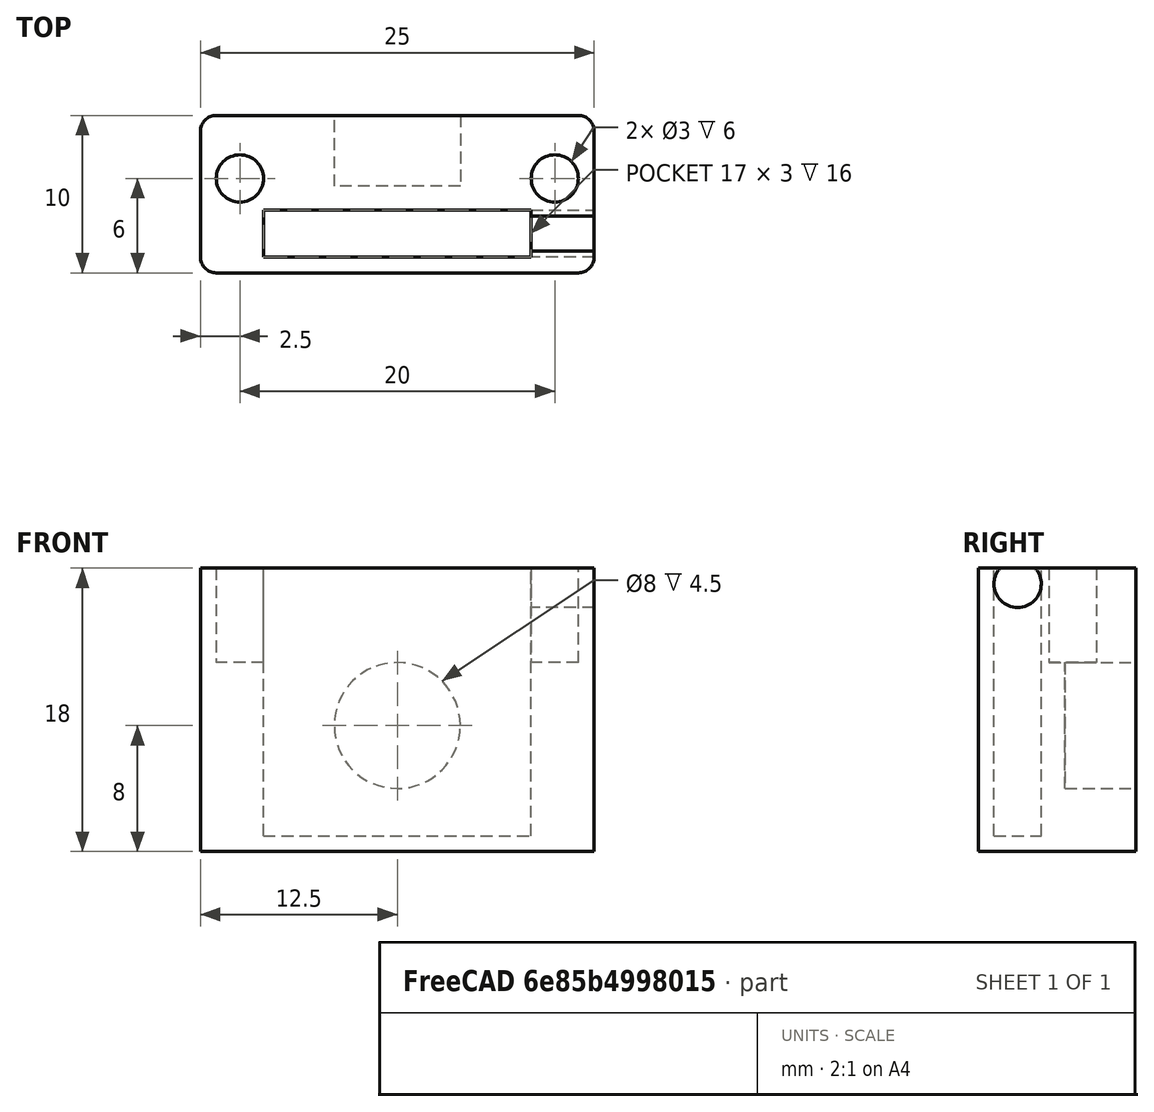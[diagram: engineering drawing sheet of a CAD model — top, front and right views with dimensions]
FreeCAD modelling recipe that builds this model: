
FCSTD DOCUMENT  (FreeCAD 0.20R29603 (Git))
Label: sensor_enclosure
License: All rights reserved
LicenseURL: http://en.wikipedia.org/wiki/All_rights_reserved
objects: PartDesign::SubtractiveCylinder×4, PartDesign::AdditiveBox×1, PartDesign::SubtractiveBox×1, PartDesign::Fillet×1, PartDesign::Body×1, App::Part×1
note: 15 computed .brp shape members not serialized (recipe doc carries the construction recipe); baked Part::Feature solids carry a one-line shape summary decoded from their .brp

FEATURE [PartDesign::AdditiveBox] Box  label="MainBox"
  AttacherType = Attacher::AttachEngine3D
  Height = 18
  Length = 25
  Width = 10
FEATURE [PartDesign::SubtractiveBox] Box001  label="PCBhole"
  AttacherType = Attacher::AttachEngine3D
  AttachmentOffset = pos=(4,1,1) rot=(0,0,1;0rad)
  BaseFeature = -> Box
  Height = 17
  Length = 17
  MapMode = 5
  Placement = pos=(4,1,1) rot=(0,0,1;0rad)
  Support = -> [XY_Plane]
  Width = 3
FEATURE [PartDesign::SubtractiveCylinder] Cylinder  label="Magnethole"
  Angle = 360
  AttacherType = Attacher::AttachEngine3D
  AttachmentOffset = pos=(12.5,8,-10) rot=(0,0,1;0rad)
  BaseFeature = -> Box001
  FirstAngle = 0
  Height = 4.5
  MapMode = 5
  Placement = pos=(12.5,10,8) rot=(1,0,0;1.5708rad)
  Radius = 4
  SecondAngle = 0
  Support = -> [XZ_Plane]
FEATURE [PartDesign::SubtractiveCylinder] Cylinder001  label="Threadinsert1"
  Angle = 360
  AttacherType = Attacher::AttachEngine3D
  AttachmentOffset = pos=(2.5,6,12) rot=(0,0,1;0rad)
  BaseFeature = -> Cylinder
  FirstAngle = 0
  Height = 6
  MapMode = 5
  Placement = pos=(2.5,6,12) rot=(0,0,1;0rad)
  Radius = 1.5
  SecondAngle = 0
  Support = -> [XY_Plane]
FEATURE [PartDesign::SubtractiveCylinder] Cylinder002  label="Threadinsert2"
  Angle = 360
  AttacherType = Attacher::AttachEngine3D
  AttachmentOffset = pos=(22.5,6,12) rot=(0,0,1;0rad)
  BaseFeature = -> Cylinder001
  FirstAngle = 0
  Height = 6
  MapMode = 5
  Placement = pos=(22.5,6,12) rot=(0,0,1;0rad)
  Radius = 1.5
  SecondAngle = 0
  Support = -> [XY_Plane]
FEATURE [PartDesign::SubtractiveCylinder] Cylinder003  label="Cablehole"
  Angle = 360
  AttacherType = Attacher::AttachEngine3D
  AttachmentOffset = pos=(2.5,17,18) rot=(0,0,1;0rad)
  BaseFeature = -> Cylinder002
  FirstAngle = 0
  Height = 10
  MapMode = 5
  Placement = pos=(18,2.5,17) rot=(0.57735,0.57735,0.57735;2.0944rad)
  Radius = 1.5
  SecondAngle = 0
  Support = -> [YZ_Plane]
FEATURE [PartDesign::Fillet] Fillet
  Base = -> Cylinder003 [Edge6,Edge21,Edge3,Edge1]
  BaseFeature = -> Cylinder003
  Placement = pos=(18,2.5,17) rot=(0.57735,0.57735,0.57735;2.0944rad)
  Radius = 1
  SupportTransform = false
  UseAllEdges = false
FEATURE [PartDesign::Body] Body
  Group = -> [Box,Box001,Cylinder,Cylinder001,Cylinder002,Cylinder003,Fillet]
  Origin = -> Origin
  Tip = -> Fillet
FEATURE [App::Part] Part
  Group = -> [Body]
  Origin = -> Origin001
